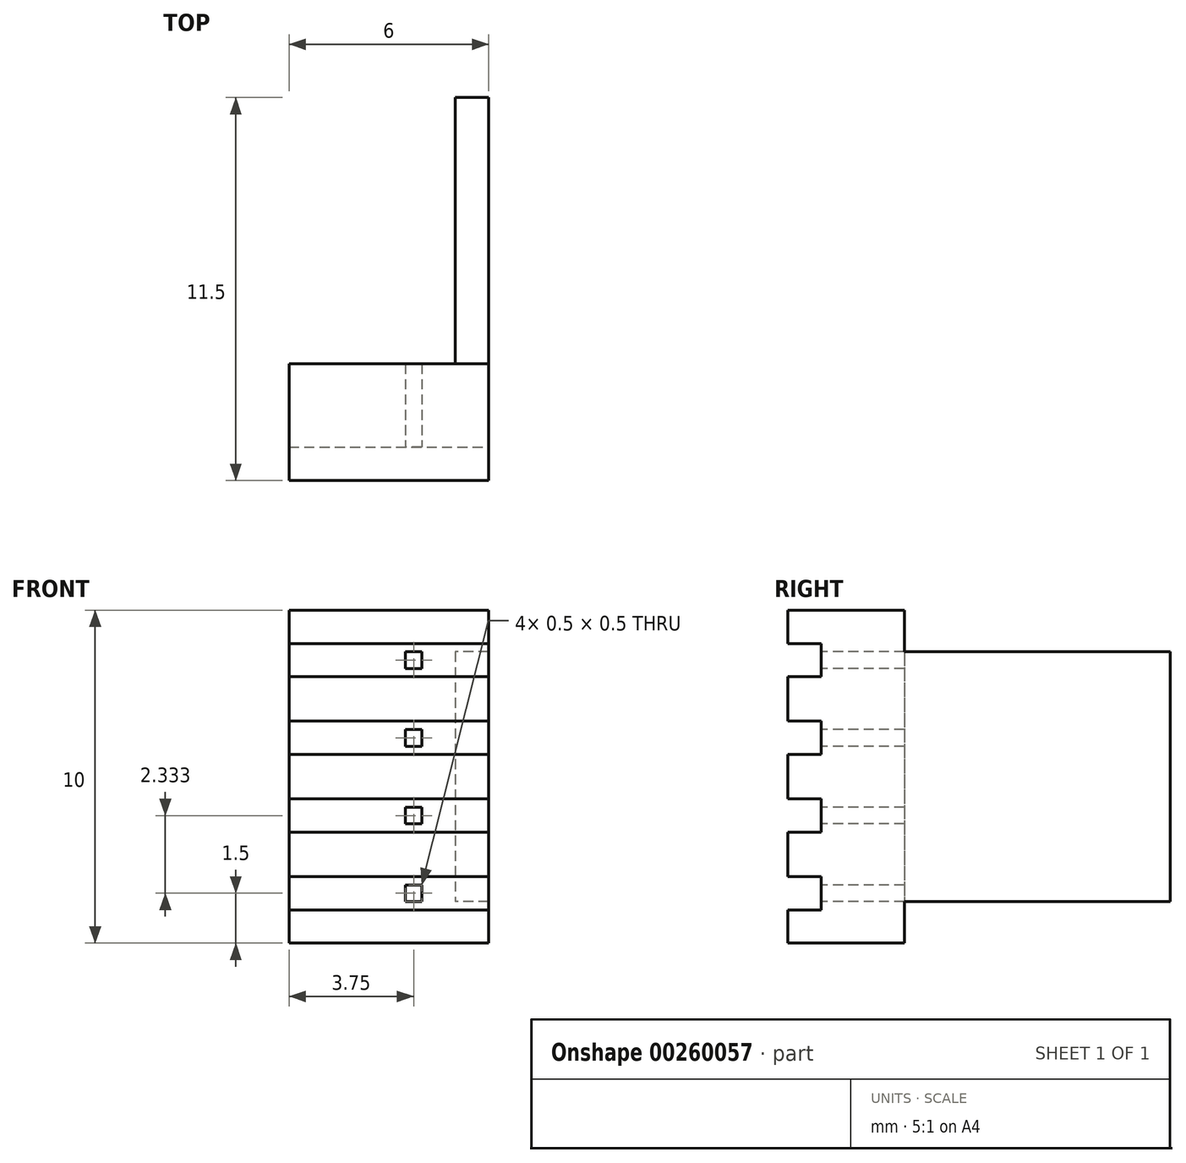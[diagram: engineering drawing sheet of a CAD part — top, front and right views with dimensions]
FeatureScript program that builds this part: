
annotation { "Feature Type Name" : "Feature", "Feature Type Description" : "" }
export const myFeature = defineFeature(function(context is Context, id is Id, definition is map)
    precondition{}
    {
        {
            var Q0;
            Q0=qCreatedBy(makeId("Top.planeOp"),FACE);
            var sketch = newSketch(context, id + "F0", { "sketchPlane" : qUnion([Q0])});
            skLineSegment(sketch, "E0.bottom", {"start": v(0, 0) * mm, "end": v(6, 0) * mm});
            skLineSegment(sketch, "E0.top", {"start": v(5, 11.5) * mm, "end": v(6, 11.5) * mm});
            skLineSegment(sketch, "E0.left", {"start": v(0, 0) * mm, "end": v(0, 3.5) * mm});
            skLineSegment(sketch, "E0.right", {"start": v(6, 0) * mm, "end": v(6, 11.5) * mm});
            skLineSegment(sketch, "E1", {"start": v(5, 11.5) * mm, "end": v(5, 3.5) * mm});
            skLineSegment(sketch, "E2", {"start": v(5, 3.5) * mm, "end": v(0, 3.5) * mm});
            skSolve(sketch);
        }
        {
            var Q0;
            Q0=qSketchRegion(id+"F0",true);
            extrude(context, id + "F1", {"entities" : qUnion([Q0]), "depth" : 10 * mm});
        }
        {
            var Q0;
            Q0=makeQuery(id+"F1.opExtrude","SWEPT_FACE",FACE,{"disambiguationData":[OSD([sQuery(id+"F0.wireOp",EDGE,"E1")])]});
            var sketch = newSketch(context, id + "F2", { "sketchPlane" : qUnion([Q0])});
            skLineSegment(sketch, "E3.bottom", {"start": v(-11.5, 0) * mm, "end": v(-3.5, 0) * mm});
            skLineSegment(sketch, "E3.top", {"start": v(-11.5, 1.25) * mm, "end": v(-3.5, 1.25) * mm});
            skLineSegment(sketch, "E3.left", {"start": v(-11.5, 0) * mm, "end": v(-11.5, 1.25) * mm});
            skLineSegment(sketch, "E3.right", {"start": v(-3.5, 0) * mm, "end": v(-3.5, 1.25) * mm});
            skLineSegment(sketch, "E4.bottom", {"start": v(-11.5, 10) * mm, "end": v(-3.5, 10) * mm});
            skLineSegment(sketch, "E4.top", {"start": v(-11.5, 8.75) * mm, "end": v(-3.5, 8.75) * mm});
            skLineSegment(sketch, "E4.left", {"start": v(-11.5, 10) * mm, "end": v(-11.5, 8.75) * mm});
            skLineSegment(sketch, "E4.right", {"start": v(-3.5, 10) * mm, "end": v(-3.5, 8.75) * mm});
            skSolve(sketch);
        }
        {
            var Q0;
            Q0=qSketchRegion(id+"F2",true);
            extrude(context, id + "F3", {"entities" : qUnion([Q0]), "operationType" : NewBodyOperationType.REMOVE, "oppositeDirection" : true, "depth" : 25 * mm});
        }
        {
            var Q0;
            Q0=makeQuery(id+"F1.opExtrude","SWEPT_FACE",FACE,{"disambiguationData":[OSD([sQuery(id+"F0.wireOp",EDGE,"E0.bottom")])]});
            var sketch = newSketch(context, id + "F4", { "sketchPlane" : qUnion([Q0])});
            skLineSegment(sketch, "E5.bottom", {"start": v(3.5, 8.75) * mm, "end": v(4, 8.75) * mm});
            skLineSegment(sketch, "E5.top", {"start": v(3.5, 1.25) * mm, "end": v(4, 1.25) * mm});
            skLineSegment(sketch, "E5.left", {"start": v(3.5, 8.75) * mm, "end": v(3.5, 8.25) * mm});
            skLineSegment(sketch, "E5.right", {"start": v(4, 8.75) * mm, "end": v(4, 8.25) * mm});
            skLineSegment(sketch, "E6", {"start": v(3.5, 8.25) * mm, "end": v(4, 8.25) * mm});
            skLineSegment(sketch, "E7", {"start": v(3.5, 6.42) * mm, "end": v(4, 6.42) * mm});
            skLineSegment(sketch, "E8", {"start": v(3.5, 5.92) * mm, "end": v(4, 5.92) * mm});
            skLineSegment(sketch, "E9", {"start": v(3.5, 4.08) * mm, "end": v(4, 4.08) * mm});
            skLineSegment(sketch, "E10", {"start": v(3.5, 3.58) * mm, "end": v(4, 3.58) * mm});
            skLineSegment(sketch, "E11", {"start": v(3.5, 1.75) * mm, "end": v(4, 1.75) * mm});
            skLineSegment(sketch, "E12.trimOffspring", {"start": v(3.5, 1.75) * mm, "end": v(3.5, 1.25) * mm});
            skLineSegment(sketch, "E13.trimOffspring", {"start": v(4, 1.75) * mm, "end": v(4, 1.25) * mm});
            skLineSegment(sketch, "E14.trimOffspring", {"start": v(3.5, 4.08) * mm, "end": v(3.5, 3.58) * mm});
            skLineSegment(sketch, "E15.trimOffspring", {"start": v(4, 4.08) * mm, "end": v(4, 3.58) * mm});
            skLineSegment(sketch, "E16.trimOffspring", {"start": v(3.5, 6.42) * mm, "end": v(3.5, 5.92) * mm});
            skLineSegment(sketch, "E17.trimOffspring", {"start": v(4, 6.42) * mm, "end": v(4, 5.92) * mm});
            skSolve(sketch);
        }
        {
            var Q0;
            Q0=qSketchRegion(id+"F4",true);
            extrude(context, id + "F5", {"entities" : qUnion([Q0]), "operationType" : NewBodyOperationType.REMOVE, "oppositeDirection" : true, "depth" : 25 * mm});
        }
        {
            var Q0;
            Q0=makeQuery(id+"F1.opExtrude","SWEPT_FACE",FACE,{"disambiguationData":[OSD([sQuery(id+"F0.wireOp",EDGE,"E0.bottom")])]});
            var sketch = newSketch(context, id + "F6", { "sketchPlane" : qUnion([Q0])});
            skLineSegment(sketch, "E18.bottom", {"start": v(0, 9) * mm, "end": v(6, 9) * mm});
            skLineSegment(sketch, "E18.top", {"start": v(0, 8) * mm, "end": v(6, 8) * mm});
            skLineSegment(sketch, "E18.left", {"start": v(0, 9) * mm, "end": v(0, 8) * mm});
            skLineSegment(sketch, "E18.right", {"start": v(6, 9) * mm, "end": v(6, 8) * mm});
            skLineSegment(sketch, "E19.bottom", {"start": v(0, 6.67) * mm, "end": v(6, 6.67) * mm});
            skLineSegment(sketch, "E19.top", {"start": v(0, 5.67) * mm, "end": v(6, 5.67) * mm});
            skLineSegment(sketch, "E19.left", {"start": v(0, 6.67) * mm, "end": v(0, 5.67) * mm});
            skLineSegment(sketch, "E19.right", {"start": v(6, 6.67) * mm, "end": v(6, 5.67) * mm});
            skLineSegment(sketch, "E20.bottom", {"start": v(0, 4.33) * mm, "end": v(6, 4.33) * mm});
            skLineSegment(sketch, "E20.top", {"start": v(0, 3.33) * mm, "end": v(6, 3.33) * mm});
            skLineSegment(sketch, "E20.left", {"start": v(0, 4.33) * mm, "end": v(0, 3.33) * mm});
            skLineSegment(sketch, "E20.right", {"start": v(6, 4.33) * mm, "end": v(6, 3.33) * mm});
            skLineSegment(sketch, "E21.bottom", {"start": v(0, 2) * mm, "end": v(6, 2) * mm});
            skLineSegment(sketch, "E21.top", {"start": v(0, 1) * mm, "end": v(6, 1) * mm});
            skLineSegment(sketch, "E21.left", {"start": v(0, 2) * mm, "end": v(0, 1) * mm});
            skLineSegment(sketch, "E21.right", {"start": v(6, 2) * mm, "end": v(6, 1) * mm});
            skSolve(sketch);
        }
        {
            var Q0;
            Q0=qSketchRegion(id+"F6",true);
            extrude(context, id + "F7", {"entities" : qUnion([Q0]), "operationType" : NewBodyOperationType.REMOVE, "oppositeDirection" : true, "depth" : 1 * mm});
        }
    });
